# Revit family: P3000SL
name_source: partatom
category: Generic Models
units: mm (PartAtom-declared; Revit-internal decimal feet)

## family parameters
Can host rebar = No
Cut with Voids When Loaded = No
Part Type = Normal
Room Calculation Point = No
Round Connector Dimension = Use Diameter
Shared = No

## types (4) — shared parameters
Description = P3000SL - 1-5/8" x 1-3/8", 12 Gauge; Long Slots - GenericModels
Height = 1.375"
Manufacturer = Atkore Unistrut
Model = P3000SL
Salsify ID1 = US-P3000SL
URL = https://www.atkore.com
zero-valued in all types: Default Elevation

## per-type parameters (varying)
| type | Material | Power-Strut Part Number | UPC-10ft | UPC-20ft | Unit Weight |
| P3000SL GR | Green |  | "786364033518" | "786364033556" | 1.7 lb/ft |
| P3000SL PL | Plain |  | "786364033549" | "786364033587" | 1.65 lb/ft |
| P3000SL HG | Hot Dip Galvanized |  | "786364033525" | "786364033563" | 1.65 lb/ft |
| P3000SL PG | Pre-Galvanized | PS 300 S PGAL | "0786364033532" | "786364033570" | 1.7 lb/ft |

note: column(s) folded — value = type name in every type: Part Number

## geometry (parser evidence)
native form markers: Sweep x8
no freeform markers — native parametric forms only
